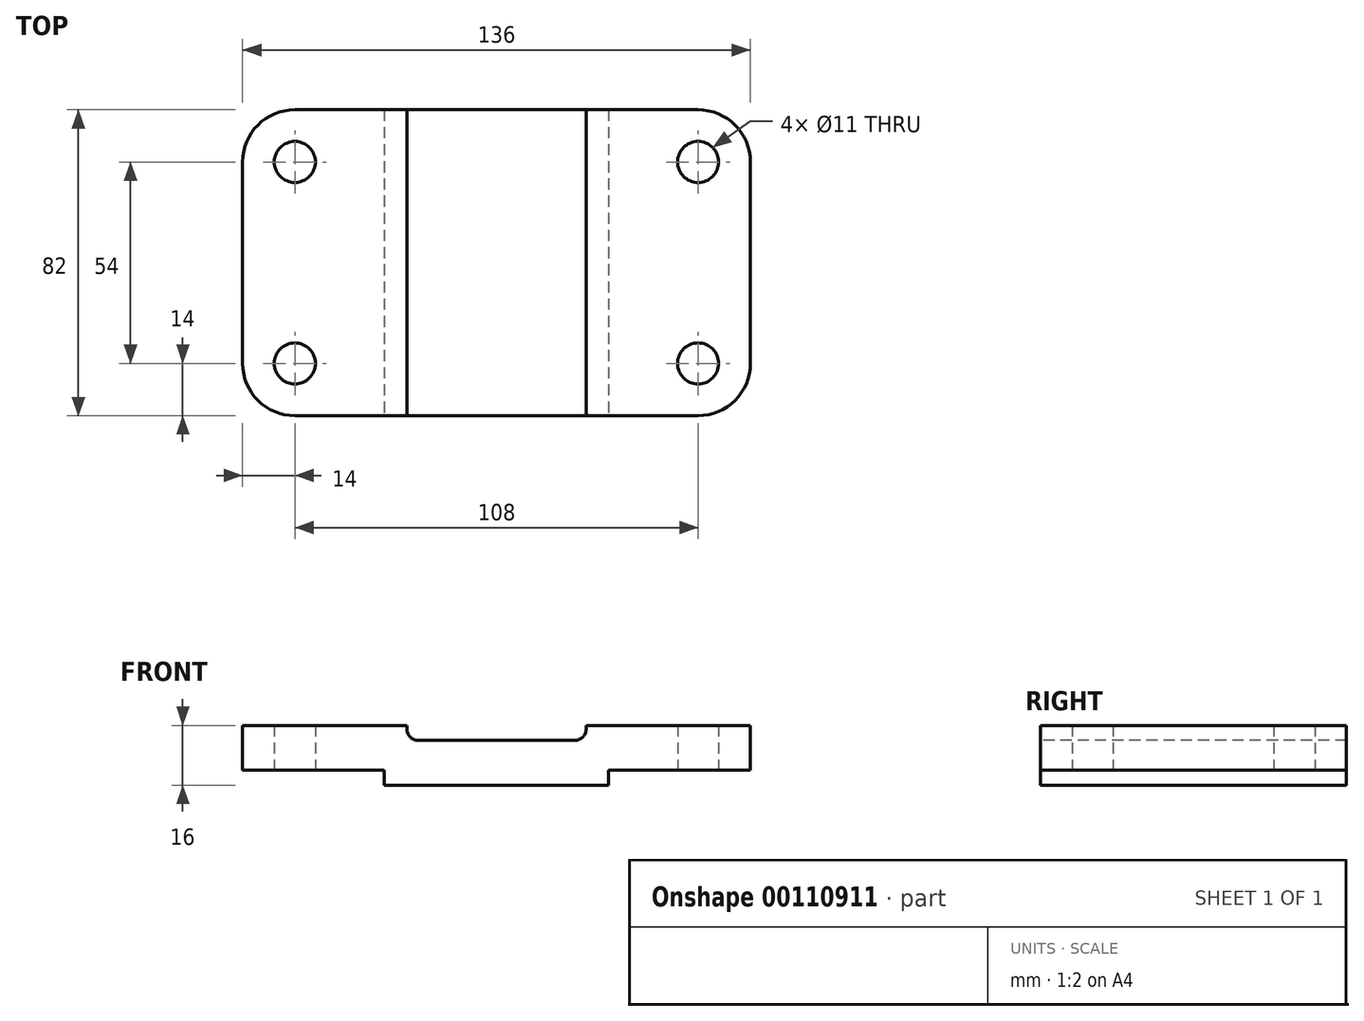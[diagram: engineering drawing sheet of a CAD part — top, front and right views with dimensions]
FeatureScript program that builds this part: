
annotation { "Feature Type Name" : "Feature", "Feature Type Description" : "" }
export const myFeature = defineFeature(function(context is Context, id is Id, definition is map)
    precondition{}
    {
        {
            var Q0;
            Q0=qCreatedBy(makeId("Top.planeOp"),FACE);
            var sketch = newSketch(context, id + "F0", { "sketchPlane" : qUnion([Q0])});
            skLineSegment(sketch, "E0.bottom", {"start": v(0, 0) * mm, "end": v(-54, 0) * mm});
            skLineSegment(sketch, "E0.top", {"start": v(0, 82) * mm, "end": v(-54, 82) * mm});
            skLineSegment(sketch, "E0.left", {"start": v(0, 0) * mm, "end": v(0, 82) * mm});
            skLineSegment(sketch, "E0.right", {"start": v(-68, 14) * mm, "end": v(-68, 68) * mm});
            skPoint(sketch, "E1.visualSharp", {"position": v(-68, 0) * mm});
            skArc(sketch, "E1.filletArc", {"start": v(-68, 14) * mm, "mid": v(-63.9, 4.1) * mm, "end": v(-54, 0) * mm});
            skPoint(sketch, "E2.visualSharp", {"position": v(-68, 82) * mm});
            skArc(sketch, "E2.filletArc", {"start": v(-54, 82) * mm, "mid": v(-63.9, 77.9) * mm, "end": v(-68, 68) * mm});
            skCircle(sketch, "E3", {"center": v(-54, 14) * mm, "radius": 5.5 * mm});
            skCircle(sketch, "E4", {"center": v(-54, 68) * mm, "radius": 5.5 * mm});
            skLineSegment(sketch, "E5", {"start": v(-54, 0) * mm, "end": v(-54, 82) * mm, "construction": true});
            skLineSegment(sketch, "E6", {"start": v(-68, 14) * mm, "end": v(0, 14) * mm, "construction": true});
            skLineSegment(sketch, "E7", {"start": v(-68, 68) * mm, "end": v(0, 68) * mm, "construction": true});
            skSolve(sketch);
        }
        {
            var Q0;
            Q0 = qSketchRegion(id + "F0", true);
            extrude(context, id + "F1", {"entities" : qUnion([Q0]), "depth" : 16 * mm});
        }
        {
            var Q0;
            Q0=qCreatedBy(makeId("Front.planeOp"),FACE);
            var sketch = newSketch(context, id + "F2", { "sketchPlane" : qUnion([Q0])});
            skLineSegment(sketch, "E8.bottom", {"start": v(-68, 0) * mm, "end": v(-30, 0) * mm});
            skLineSegment(sketch, "E8.top", {"start": v(-68, 4) * mm, "end": v(-30, 4) * mm});
            skLineSegment(sketch, "E8.left", {"start": v(-68, 0) * mm, "end": v(-68, 4) * mm});
            skLineSegment(sketch, "E8.right", {"start": v(-30, 0) * mm, "end": v(-30, 4) * mm});
            skSolve(sketch);
        }
        {
            var Q0;
            Q0 = qSketchRegion(id + "F2", true);
            extrude(context, id + "F3", {"entities" : qUnion([Q0]), "operationType" : NewBodyOperationType.REMOVE, "endBound" : BoundingType.THROUGH_ALL, "oppositeDirection" : true, "depth" : 25 * mm});
        }
        {
            var Q0;
            Q0=qCreatedBy(makeId("Front.planeOp"),FACE);
            var sketch = newSketch(context, id + "F4", { "sketchPlane" : qUnion([Q0])});
            skPoint(sketch, "E9", {"position": v(-24, 16) * mm});
            skLineSegment(sketch, "E10.bottom", {"start": v(-24, 16) * mm, "end": v(0, 16) * mm});
            skLineSegment(sketch, "E10.top", {"start": v(-21, 12) * mm, "end": v(0, 12) * mm});
            skLineSegment(sketch, "E10.left", {"start": v(-24, 16) * mm, "end": v(-24, 15) * mm});
            skLineSegment(sketch, "E10.right", {"start": v(0, 16) * mm, "end": v(0, 12) * mm});
            skPoint(sketch, "E11.visualSharp", {"position": v(-24, 12) * mm});
            skArc(sketch, "E11.filletArc", {"start": v(-24, 15) * mm, "mid": v(-23.12, 12.88) * mm, "end": v(-21, 12) * mm});
            skSolve(sketch);
        }
        {
            var Q0;
            Q0 = qSketchRegion(id + "F4", true);
            extrude(context, id + "F5", {"entities" : qUnion([Q0]), "operationType" : NewBodyOperationType.REMOVE, "endBound" : BoundingType.THROUGH_ALL, "oppositeDirection" : true, "depth" : 25 * mm});
        }
        {
            var Q0;
            Q0=makeQuery(id+"F1.opExtrude","SWEPT_BODY",BODY,{"disambiguationData":[OSD([sQuery(id+"F0.wireOp",EDGE,"E0.bottom"),sQuery(id+"F0.wireOp",EDGE,"E0.top"),sQuery(id+"F0.wireOp",EDGE,"E0.left"),sQuery(id+"F0.wireOp",EDGE,"E0.right"),sQuery(id+"F0.wireOp",EDGE,"E1.filletArc"),sQuery(id+"F0.wireOp",EDGE,"E2.filletArc"),sQuery(id+"F0.wireOp",EDGE,"E3"),sQuery(id+"F0.wireOp",EDGE,"E4")])]});
            var Q1;
            Q1=qCreatedBy(makeId("Right.planeOp"),FACE);
            mirror(context, id + "F6", {"operationType" : NewBodyOperationType.ADD, "entities" : qUnion([Q0]), "mirrorPlane" : qUnion([Q1])});
        }
    });
